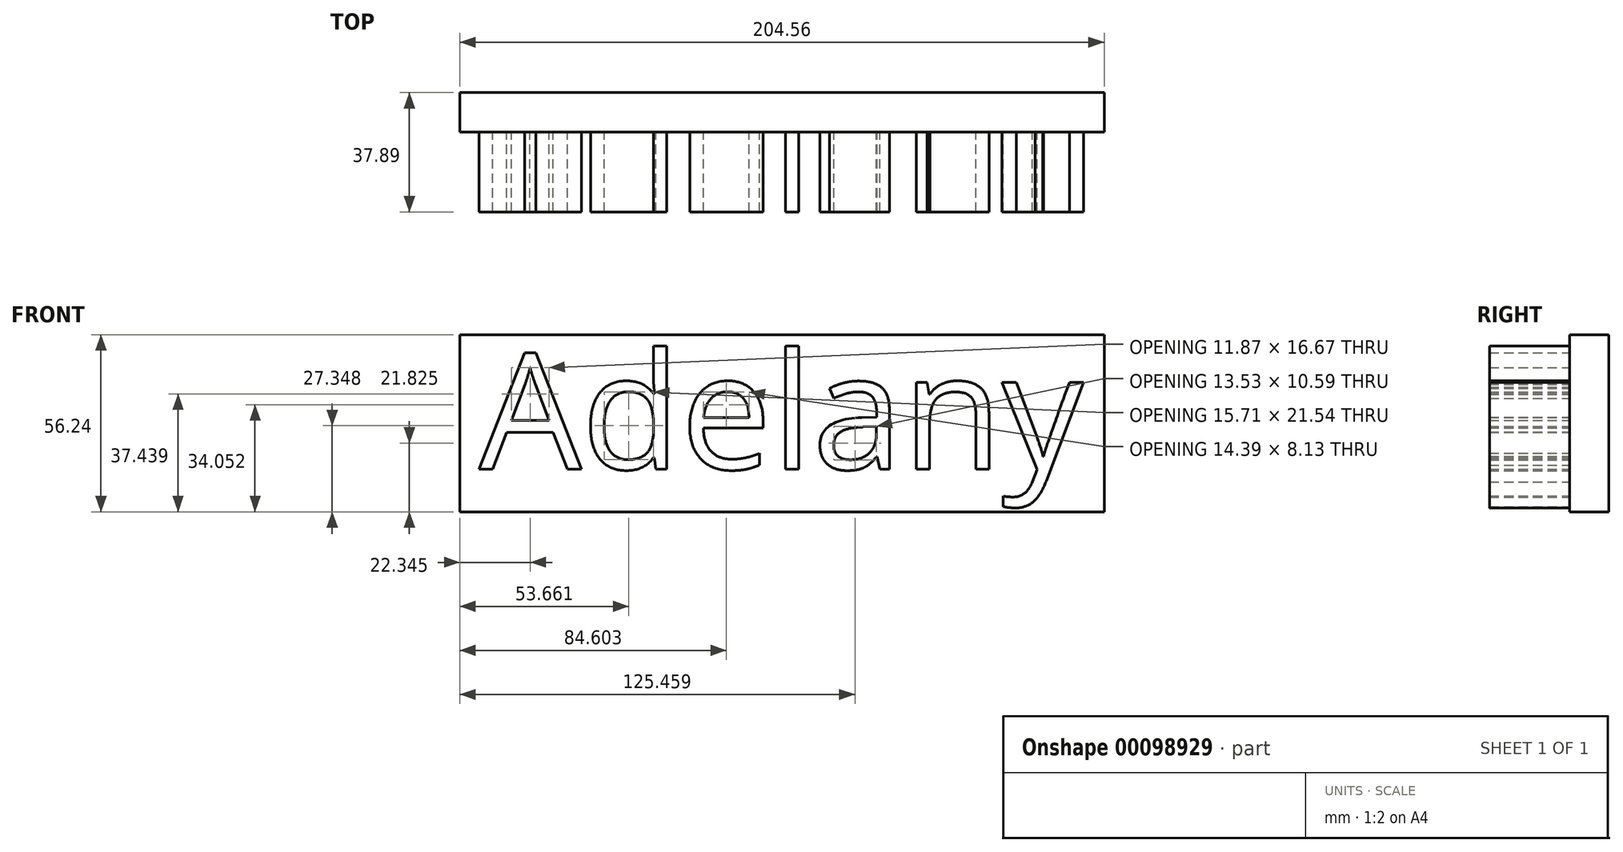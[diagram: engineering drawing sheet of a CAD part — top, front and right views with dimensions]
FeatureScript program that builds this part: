
annotation { "Feature Type Name" : "Feature", "Feature Type Description" : "" }
export const myFeature = defineFeature(function(context is Context, id is Id, definition is map)
    precondition{}
    {
        {
            var Q0;
            Q0=qCreatedBy(makeId("Front.planeOp"),FACE);
            var sketch = newSketch(context, id + "F0", { "sketchPlane" : qUnion([Q0])});
            skText(sketch, "E0", { "text": "Adelany", "fontName": "OpenSans-Regular.ttf"});
            const initialGuessF0  = {"E0": [-0.0738, 0.0055, 1, 0, 0.03702]};
            skSetInitialGuess(sketch, initialGuessF0);
            skSolve(sketch);
        }
        {
            var Q0;
            Q0 = qSketchRegion(id + "F0", true);
            extrude(context, id + "F1", {"entities" : qUnion([Q0]), "depth" : 25.4 * mm});
        }
        {
            var Q0;
            Q0=qCreatedBy(makeId("Front.planeOp"),FACE);
            var sketch = newSketch(context, id + "F2", { "sketchPlane" : qUnion([Q0])});
            skLineSegment(sketch, "E1.bottom", {"start": v(124.7, 48.15) * mm, "end": v(-79.86, 48.15) * mm});
            skLineSegment(sketch, "E1.top", {"start": v(124.7, -8.09) * mm, "end": v(-79.86, -8.09) * mm});
            skLineSegment(sketch, "E1.left", {"start": v(124.7, 48.15) * mm, "end": v(124.7, -8.09) * mm});
            skLineSegment(sketch, "E1.right", {"start": v(-79.86, 48.15) * mm, "end": v(-79.86, -8.09) * mm});
            skSolve(sketch);
        }
        {
            var Q0;
            Q0 = qSketchRegion(id + "F2", true);
            extrude(context, id + "F3", {"entities" : qUnion([Q0]), "oppositeDirection" : true, "depth" : 12.5 * mm});
        }
    });
